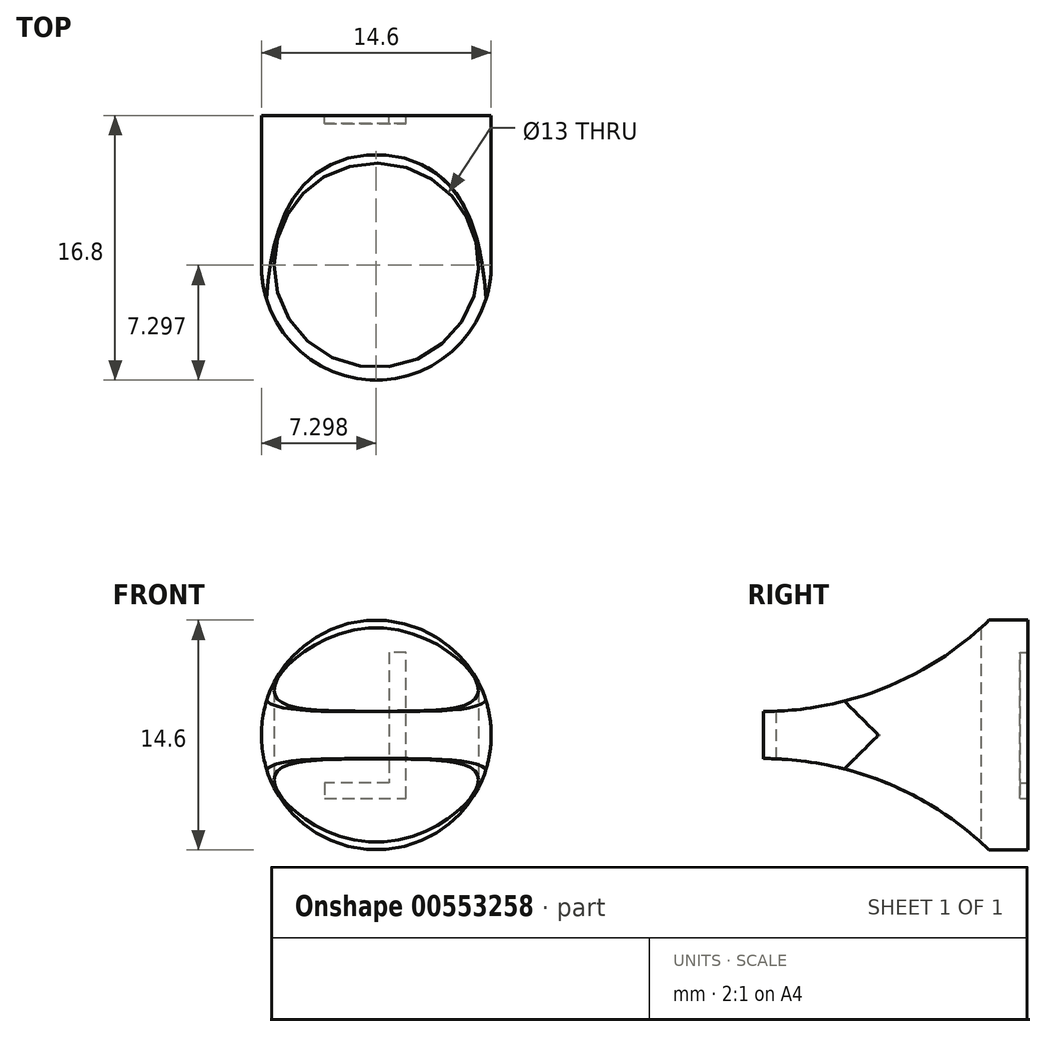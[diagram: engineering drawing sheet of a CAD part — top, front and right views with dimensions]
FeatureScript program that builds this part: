
annotation { "Feature Type Name" : "Feature", "Feature Type Description" : "" }
export const myFeature = defineFeature(function(context is Context, id is Id, definition is map)
    precondition{}
    {
        {
            assignVariable(context, id + "F0", {"name" : "SormenKoko", "anyValue" : 13});
        }
        {
            var Q0;
            Q0=qCreatedBy(makeId("Top.planeOp"),FACE);
            var sketch = newSketch(context, id + "F1", { "sketchPlane" : qUnion([Q0])});
            skCircle(sketch, "E0", {"center": v(-51.9, -6.6) * mm, "radius": 6.5 * mm});
            skArc(sketch, "E1", {"start": v(-59.2, -6.54) * mm, "mid": v(-51.93, -13.9) * mm, "end": v(-44.6, -6.6) * mm});
            skLineSegment(sketch, "E2.bottom", {"start": v(-59.2, -6.67) * mm, "end": v(-44.6, -6.67) * mm});
            skLineSegment(sketch, "E2.top", {"start": v(-59.2, 2.9) * mm, "end": v(-44.6, 2.9) * mm});
            skLineSegment(sketch, "E2.left", {"start": v(-59.2, -6.67) * mm, "end": v(-59.2, 2.9) * mm});
            skLineSegment(sketch, "E2.right", {"start": v(-44.6, -6.67) * mm, "end": v(-44.6, 2.9) * mm});
            skSolve(sketch);
        }
        {
            var Q0;
            Q0 = qSketchRegion(id + "F1", true);
            extrude(context, id + "F2", {"entities" : qUnion([Q0]), "depth" : (getVariable(context, 'SormenKoko') + 0.8 * 2) * mm, "offsetDistance" : 25 * mm});
        }
        {
            var Q0;
            Q0=makeQuery(id+"F2.opExtrude","SWEPT_FACE",FACE,{"disambiguationData":[OSD([sQuery(id+"F1.wireOp",EDGE,"E2.top")])]});
            var sketch = newSketch(context, id + "F3", { "sketchPlane" : qUnion([Q0])});
            skLineSegment(sketch, "E3", {"start": v(44.6, 14.6) * mm, "end": v(59.2, 0) * mm, "construction": true});
            skLineSegment(sketch, "E4", {"start": v(59.2, 0) * mm, "end": v(59.2, 14.6) * mm, "construction": true});
            skLineSegment(sketch, "E5", {"start": v(59.2, 14.6) * mm, "end": v(44.6, 0) * mm, "construction": true});
            skCircle(sketch, "E6", {"center": v(51.9, 7.3) * mm, "radius": 7.3 * mm});
            skCircle(sketch, "E7", {"center": v(51.9, 7.3) * mm, "radius": 25 * mm});
            skSolve(sketch);
        }
        {
            var Q0;
            Q0 = qSketchRegion(id + "F3", true);
            extrude(context, id + "F4", {"entities" : qUnion([Q0]), "operationType" : NewBodyOperationType.REMOVE, "oppositeDirection" : true, "depth" : 25 * mm, "offsetDistance" : 25 * mm});
        }
        {
            var Q0;
            Q0=qCreatedBy(makeId("Right.planeOp"),FACE);
            var sketch = newSketch(context, id + "F5", { "sketchPlane" : qUnion([Q0])});
            skLineSegment(sketch, "E8", {"start": v(2.46, 7.3) * mm, "end": v(-15.04, 7.3) * mm, "construction": true});
            skCircle(sketch, "E9", {"center": v(-13.9, 29.4) * mm, "radius": 20.6 * mm});
            skLineSegment(sketch, "E10", {"start": v(-13.9, 7.3) * mm, "end": v(-13.9, 29.4) * mm, "construction": true});
            skCircle(sketch, "E11.MirrorC", {"center": v(-13.9, -14.8) * mm, "radius": 20.6 * mm});
            skSolve(sketch);
        }
        {
            var Q0;
            Q0 = qSketchRegion(id + "F5", true);
            extrude(context, id + "F6", {"entities" : qUnion([Q0]), "operationType" : NewBodyOperationType.REMOVE, "endBound" : BoundingType.THROUGH_ALL, "oppositeDirection" : true, "depth" : 25 * mm, "offsetDistance" : 25 * mm});
        }
        {
            var Q0;
            Q0=makeQuery(id+"F2.opExtrude","SWEPT_FACE",FACE,{"disambiguationData":[OSD([sQuery(id+"F1.wireOp",EDGE,"E2.top")])]});
            var sketch = newSketch(context, id + "F7", { "sketchPlane" : qUnion([Q0])});
            skText(sketch, "E12", { "text": "L", "fontName": "OpenSans-Regular.ttf"});
            const initialGuessF7  = {"E12": [0.04873, 0.00328, 1, 0, 0.00936]};
            skSetInitialGuess(sketch, initialGuessF7);
            skSolve(sketch);
        }
        {
            var Q0;
            Q0=makeQuery(id+"F7.imprint","IMPRINT",FACE,{"disambiguationData":[TD([[makeQuery(id+"F7.imprint","IMPRINT",EDGE,{"derivedFrom":sQuery(id+"F7.wireOp",EDGE,"E12.sketch_text.stroke-0")}),-1.0]])]});
            var Q1;
            Q1 = qConstructionFilter(qBodyType(qCreatedBy(id + "F7" ,EDGE), BodyType.WIRE), ConstructionObject.NO);
            extrude(context, id + "F8", {"entities" : qUnion([Q0]), "operationType" : NewBodyOperationType.REMOVE, "surfaceEntities" : qUnion([Q1]), "oppositeDirection" : true, "depth" : 0.5 * mm, "offsetDistance" : 25 * mm});
        }
    });
